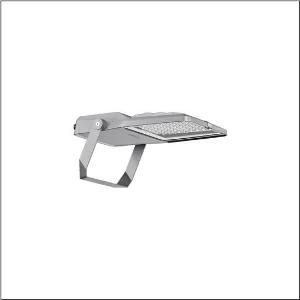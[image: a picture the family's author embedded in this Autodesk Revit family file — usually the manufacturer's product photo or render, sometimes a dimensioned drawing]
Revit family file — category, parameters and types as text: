
# Revit family: floodlight_fl_21_iq_mini___pl52_5xa7772b2d1a_4cc7
name_source: partatom
category: Lighting Fixtures
units: mm (PartAtom-declared; Revit-internal decimal feet)

## family parameters
Cut with Voids When Loaded = No
Host = Face
Light Source = No
Part Type = Normal
Room Calculation Point = No
Round Connector Dimension = Use Diameter
Shared = No

## types (1)
- --- (1 x LED, 6240 lm, 45.5 W, 3000K)
    Apparent Load = 46 VA
    CIE Flux Codes = 26 60 98 100 100
    Color Rendering = 70
    Color Temperature = 3000K
    Default Elevation = 1800 mm
    Description = Floodlight FL 21 iQ mini, floodlight, primary light control with lens, of PMMA, primary optical cover: protective disc, of toughened safety glass, transparent, light distribution: PL52, light emission: direct distribution, installation type: surface-mounted, LED, High Power LED, rated luminous flux: 6.240lm, luminous efficacy: 137lm/W, light colour: 730, colour temperature: 3000K, control: Street-Remote, Auto-Match, Temp-Guard, Night-Set, Smart-Wire, Desk-Remote (wireless, voltage-free reading and setting of iQ features in the workshop via application-optimized NFC function/RFID function), optimised constant luminous flux control (CLO 2.0), with terminal, 6-pole, mains connection: 220..240V, AC, 50/60Hz, start of lifetime: 46W, end of service life: 48W, reduction: 22W, luminaire housing, of diecast aluminium, powder-coated, Siteco® metallic grey (DB 702S), corrosivity category C5 mid according to DIN EN ISO 12944, sealing non-destructively replaceable, mounting bracket, of steel, galvanised, powder-coated, Siteco® metallic grey (DB 702S), protection rating (complete): IP66, insulation class (complete): insulation class II (safety insulation), certification: CE, ENEC, VDE, protection symbol: D, impact resistance: IK08, permissible operating ambient temperature: -40..+40°C, permissible operating ambient temperature for outdoor applications: -40..+50°C, standard: DIN EN 12944, LABS conformity tested according to VDMA 24364:2018-05, packaging unit: 1 piece

Light Distribution: PL52
    Height = 70 mm
    Lamp = 1 x LED
    Lamp Light Flux = 6240 lm
    Lamp Power = 45.5 W
    Lamp count = 1
    Length = 485 mm
    Luminous efficacy = 137 lm/W
    Manufacturer = Siteco
    ModVariant = No
    Model = 5XA7772B2D1A
    Number of Poles = 1
    OnlyDefault = Yes
    Power Factor = 1
    Product Name = Floodlight FL 21 iQ mini | PL52
    Product group = floodlight | pylon annexe
    ProductGroupID = 6200
    Protection Class = Protection class II
    Protection Degree = IP 66
    RLX_Detail_Level = 1
    RLX_Emergency_Light_Flux = 0 lm
    RLX_Emergency_Type = 0
    RLX_Emergency_Type_DB = No
    RlxData = <blob elided: 96309 chars, md5=b0d73dc7>
    Socket = socket
    Standby Power = 0 W
    System Light Flux = 6240 lm
    System Power = 46 W
    Type Comments = factory setting: luminous flux: 100 % | dim-lin: 254 | 463 mA
    Type Image = l_1006845.jpg
    URL = http://relux.com
    VarID = @adj_097215
    Voltage = 0 V
    Weight = 0.00 kg
    Width = 337 mm

## geometry (parser evidence)
native form markers: Blend x4, Sweep x12
no freeform markers — native parametric forms only
